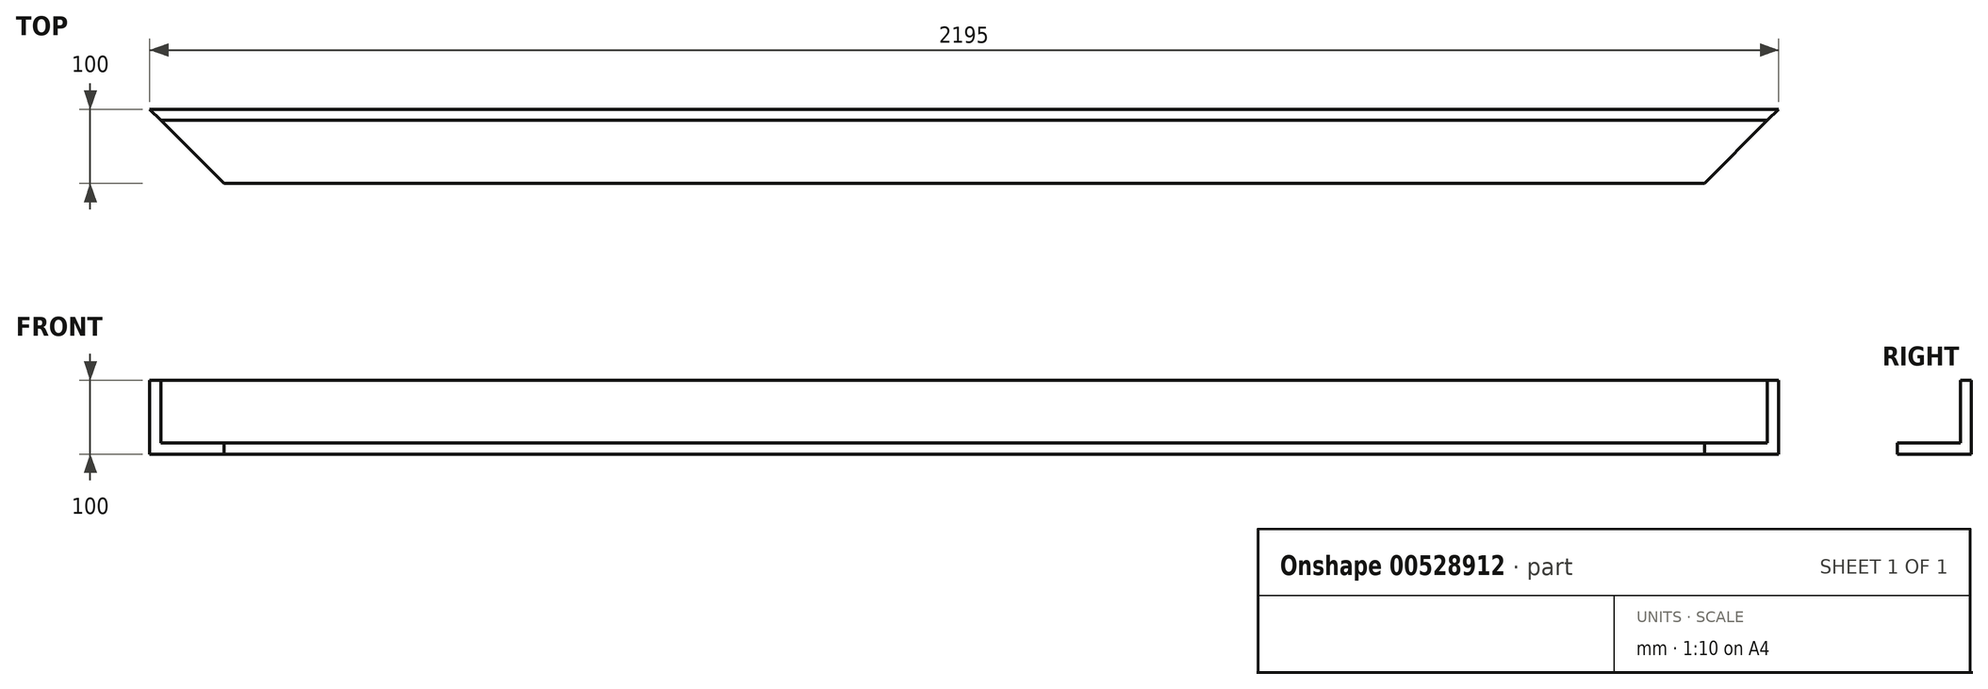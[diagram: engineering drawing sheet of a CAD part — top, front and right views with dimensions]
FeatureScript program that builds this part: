
annotation { "Feature Type Name" : "Feature", "Feature Type Description" : "" }
export const myFeature = defineFeature(function(context is Context, id is Id, definition is map)
    precondition{}
    {
        {
            var Q0;
            Q0=qCreatedBy(makeId("Top.planeOp"),FACE);
            var sketch = newSketch(context, id + "F0", { "sketchPlane" : qUnion([Q0])});
            skLineSegment(sketch, "E0", {"start": v(28.05, 0) * mm, "end": v(-28.05, 0) * mm, "construction": true});
            skLineSegment(sketch, "E1", {"start": v(1097.5, 100) * mm, "end": v(-1097.5, 100) * mm});
            skLineSegment(sketch, "E2", {"start": v(-1097.5, 100) * mm, "end": v(-997.5, 200) * mm});
            skLineSegment(sketch, "E3", {"start": v(-997.5, 200) * mm, "end": v(997.5, 200) * mm});
            skLineSegment(sketch, "E4", {"start": v(997.5, 200) * mm, "end": v(1097.5, 100) * mm});
            skLineSegment(sketch, "E5", {"start": v(0, 0) * mm, "end": v(0, 100) * mm, "construction": true});
            skSolve(sketch);
        }
        {
            var Q0;
            Q0=qSketchRegion(id+"F0",true);
            extrude(context, id + "F1", {"entities" : qUnion([Q0]), "depth" : 15 * mm, "offsetDistance" : 25 * mm});
        }
        {
            var Q0;
            Q0=makeQuery(id+"F1.opExtrude","CAP_FACE",FACE,{"disambiguationData":[OSD([sQuery(id+"F0.wireOp",EDGE,"E1"),sQuery(id+"F0.wireOp",EDGE,"E2"),sQuery(id+"F0.wireOp",EDGE,"E3"),sQuery(id+"F0.wireOp",EDGE,"E4")])],"isStart":false});
            var sketch = newSketch(context, id + "F2", { "sketchPlane" : qUnion([Q0])});
            skLineSegment(sketch, "E6.0", {"start": v(1097.5, 100) * mm, "end": v(-1097.5, 100) * mm});
            skLineSegment(sketch, "E7", {"start": v(1082.5, 115) * mm, "end": v(-1082.5, 115) * mm});
            skLineSegment(sketch, "E8", {"start": v(-1082.5, 115) * mm, "end": v(-1097.5, 100) * mm});
            skLineSegment(sketch, "E9", {"start": v(1097.5, 100) * mm, "end": v(1082.5, 115) * mm});
            skSolve(sketch);
        }
        {
            var Q0;
            Q0=makeQuery(id+"F2.imprint","IMPRINT",FACE,{"disambiguationData":[TD([[makeQuery(id+"F2.imprint","IMPRINT",EDGE,{"derivedFrom":sQuery(id+"F2.wireOp",EDGE,"E6.0")}),-1.0]])]});
            extrude(context, id + "F3", {"entities" : qUnion([Q0]), "operationType" : NewBodyOperationType.ADD, "depth" : (100 - 15) * mm, "offsetDistance" : 25 * mm});
        }
        {
            var Q0;
            Q0=makeQuery(id+"F3.boolean.opBoolean","MERGE",FACE,{"derivedFrom":[makeQuery(id+"F1.opExtrude","SWEPT_FACE",FACE,{"disambiguationData":[OSD([sQuery(id+"F0.wireOp",EDGE,"E1")])]}),makeQuery(id+"F3.opExtrude","SWEPT_FACE",FACE,{"disambiguationData":[OSD([sQuery(id+"F2.wireOp",EDGE,"E6.0")])]})]});
            cPlane(context, id + "F4", {"entities" : qUnion([Q0]), "cplaneType" : CPlaneType.OFFSET, "offset" : 1990.5 * mm, "oppositeDirection" : true, "width" : 150 * mm, "height" : 150 * mm});
        }
        {
            var Q0;
            Q0=makeQuery(id+"F1.opExtrude","SWEPT_BODY",BODY,{"disambiguationData":[OSD([sQuery(id+"F0.wireOp",EDGE,"E1"),sQuery(id+"F0.wireOp",EDGE,"E2"),sQuery(id+"F0.wireOp",EDGE,"E3"),sQuery(id+"F0.wireOp",EDGE,"E4")])]});
            var Q1;
            Q1=qCreatedBy(id+"F4.planeOp",FACE);
            mirror(context, id + "F5", {"entities" : qUnion([Q0]), "mirrorPlane" : qUnion([Q1])});
        }
        {
            var Q0;
            Q0=makeQuery(id+"F1.opExtrude","SWEPT_BODY",BODY,{"disambiguationData":[OSD([sQuery(id+"F0.wireOp",EDGE,"E1"),sQuery(id+"F0.wireOp",EDGE,"E2"),sQuery(id+"F0.wireOp",EDGE,"E3"),sQuery(id+"F0.wireOp",EDGE,"E4")])]});
            deleteBodies(context, id + "F6", {"entities" : qUnion([Q0])});
        }
    });
